# Revit family: Pearl Cluster 15W
name_source: partatom
category: Lighting Fixtures
revit_build: Autodesk Revit 2017 (Build: 20160225_1515(x64)
units: mm (PartAtom-declared; Revit-internal decimal feet)

## family parameters
Cut with Voids When Loaded = No
Host = Face
Light Source = No
OmniClass Number = 23.80.70.11.11
OmniClass Title = General Luminaries, Non Directional
Part Type = Normal
Room Calculation Point = No
Round Connector Dimension = Use Diameter
Shared = No

## types (2) — shared parameters
Beam Angle = 160°
CRI = 82
Casing Color = White
Color Temperature = 4000K
Cutout = -
Default Elevation = 1219 mm
Depth = -
Description = Pendant Light
Dimensions = 150mm x 1500mm
Dimmable = Yes
Directivity = No
Driver = Integrated
Housing Material = Aluminium
IP Code = IP20
Lamp = LED
Last Updated = 8.4.2017
Lifetime L70 = 50000h
Manufacturer = Winled Oy Ltd
Model = Pear Cluster 15W
Operating Temperature Range = -20° to +50°
Type Image = Pearl Cluster .png
URL = www.winled.fi
Voltage = 230 V
Wattage Comments = 15W

## per-type parameters (varying)
| type | Light source | Lumens Output | Product Number |
| Pearl Cluster 15W, Neutral White, 230V - 53SI995N015J | Pearl light NV | 1264lm | 53SI995N015J |
| Pearl Cluster 15W, Warm White, 230V - 53SI995L015J | Pearl light LV | 1164lm | 53SI995L015J |

## geometry (parser evidence)
native form markers: Sweep x14
no freeform markers — native parametric forms only
